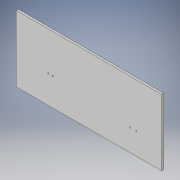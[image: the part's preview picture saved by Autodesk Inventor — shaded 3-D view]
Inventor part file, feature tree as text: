
AUTODESK INVENTOR PART (.ipt)
format: ipt  version: 2017 (Build 210142000, 142)  size: 122,368 bytes
history: native  units: in
note: dims shown in document units (in); Inventor stores cm internally (conversion verified against a paired STEP export)
features: sketch x3, hole x2, extrude x1, thicken_offset x1
ambient origin geometry x8: Origin, YZ Plane, XZ Plane, XY Plane, X Axis, Y Axis, Z Axis, Center Point
bodies: Solid1 (feature_tree)
feature tree (7):
  extrude  "Extrusion1"  Depth=6.0in
  thicken_offset  "Thicken1"
  hole  "Hole1"  [1 undecoded]
  hole  "Hole2"  [1 undecoded]
  sketch  "Sketch1"  dims[d0=17.0in d1=6.0in]
  sketch  "Sketch3"  dims[d2=0.25in d3=0.0in d4=1.75in]
  sketch  "Sketch5"  dims[d5=1.75in d8=3.06in d9=90.0deg d10=3.5in d11=1.0in d12=0.375in d13=0.25in d14=0.25in d15=0.13in d16=0.75in d17=0.375in d18=0.25in d19=0.5635in d20=1.0in d21=0.8108in d22=2.45in d23=0.0in d24=2.35in d25=90.0deg d26=0.0in d27=1.75in d28=0.375in d29=0.5in d30=0.5in d31=0.13in d32=0.75in d33=0.375in d34=0.25in d35=0.5635in d36=1.0in d37=0.8108in]
note: 2 required parameter values undecoded (feature->parameter linkage not recoverable at this tier; creation-order binding heuristic only, values carry confidence <= 0.55)
